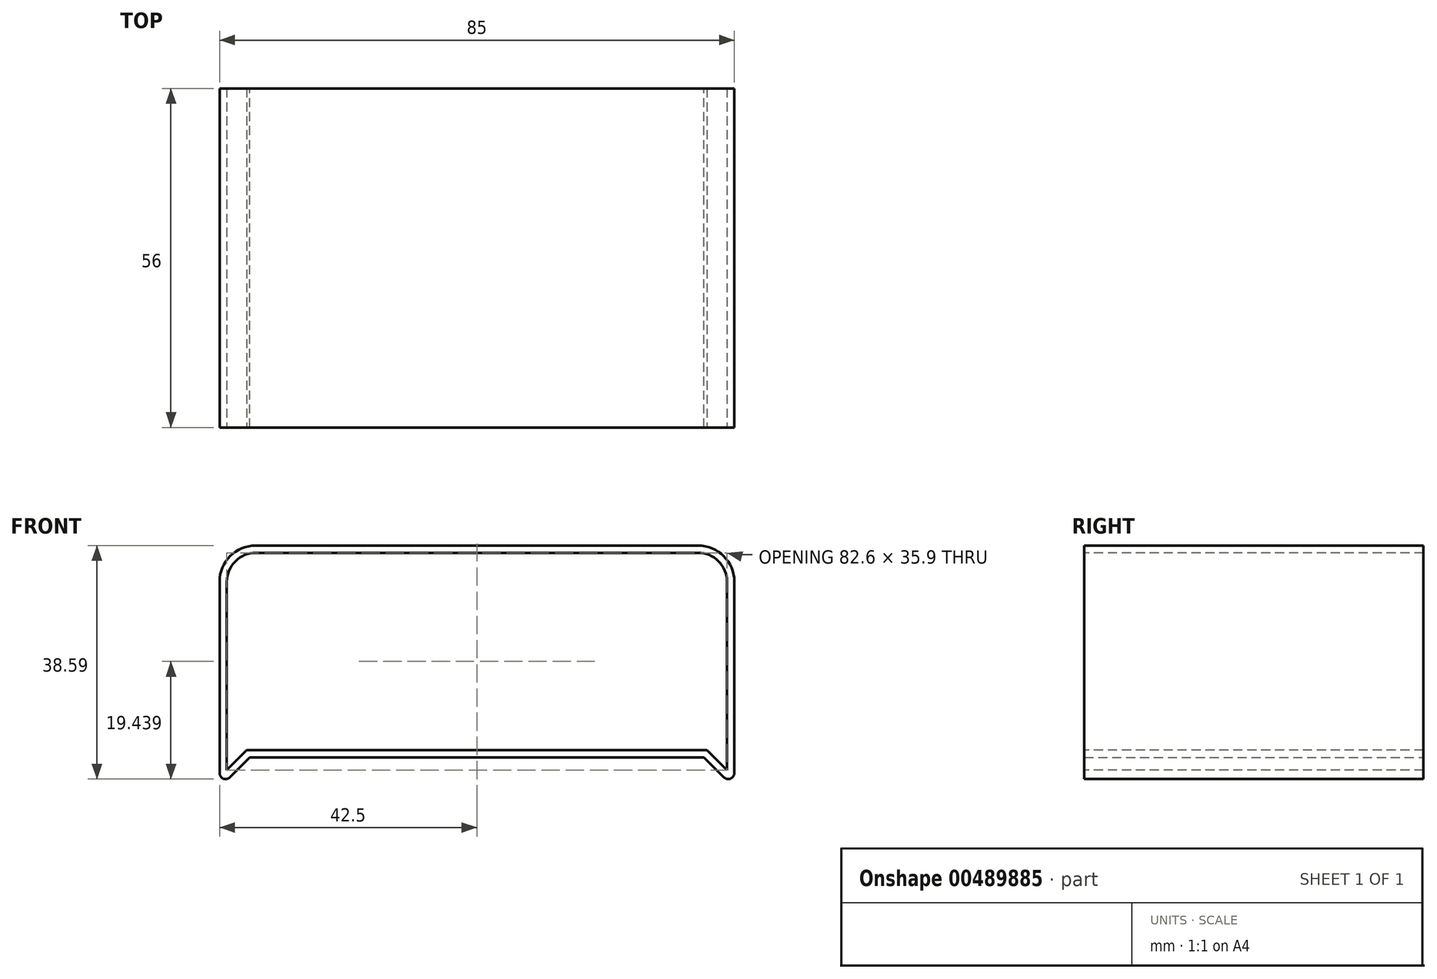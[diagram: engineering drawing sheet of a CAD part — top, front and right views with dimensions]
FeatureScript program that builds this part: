
annotation { "Feature Type Name" : "Feature", "Feature Type Description" : "" }
export const myFeature = defineFeature(function(context is Context, id is Id, definition is map)
    precondition{}
    {
        {
            var Q0;
            Q0=qCreatedBy(makeId("Front.planeOp"),FACE);
            var sketch = newSketch(context, id + "F0", { "sketchPlane" : qUnion([Q0])});
            skLineSegment(sketch, "E0.bottom", {"start": v(-42.5, 17.5) * mm, "end": v(42.5, 17.5) * mm});
            skLineSegment(sketch, "E0.top", {"start": v(-42.5, -17.5) * mm, "end": v(42.5, -17.5) * mm});
            skLineSegment(sketch, "E0.left", {"start": v(-42.5, 17.5) * mm, "end": v(-42.5, -17.5) * mm});
            skLineSegment(sketch, "E0.right", {"start": v(42.5, 17.5) * mm, "end": v(42.5, -17.5) * mm});
            skPoint(sketch, "E0.middle", {"position": v(0, 0) * mm});
            skLineSegment(sketch, "E1", {"start": v(-42.5, -17.5) * mm, "end": v(-42.5, -22.5) * mm});
            skLineSegment(sketch, "E2", {"start": v(-42.5, -22.5) * mm, "end": v(-37.5, -17.5) * mm});
            skLineSegment(sketch, "E3", {"start": v(42.5, -17.5) * mm, "end": v(42.5, -22.5) * mm});
            skLineSegment(sketch, "E4", {"start": v(42.5, -22.5) * mm, "end": v(37.5, -17.5) * mm});
            skSolve(sketch);
        }
        {
            var Q0;
            Q0 = qSketchRegion(id + "F0", true);
            extrude(context, id + "F1", {"entities" : qUnion([Q0]), "depth" : 56 * mm});
        }
        {
            var Q0;
            Q0=makeQuery(id+"F1.opExtrude","SWEPT_EDGE",EDGE,{"disambiguationData":[OSD([sQuery(id+"F0.wireOp",EDGE,"E1"),sQuery(id+"F0.wireOp",EDGE,"E2")])]});
            var Q1;
            Q1=makeQuery(id+"F1.opExtrude","SWEPT_EDGE",EDGE,{"disambiguationData":[OSD([sQuery(id+"F0.wireOp",EDGE,"E3"),sQuery(id+"F0.wireOp",EDGE,"E4")])]});
            fillet(context, id + "F2", {"entities" : qUnion([Q0, Q1]), "radius" : 1 * mm, "tangentPropagation" : true, "allowEdgeOverflow" : false});
        }
        {
            var Q0;
            Q0=makeQuery(id+"F1.opExtrude","SWEPT_EDGE",EDGE,{"disambiguationData":[OSD([sQuery(id+"F0.wireOp",EDGE,"E0.bottom"),sQuery(id+"F0.wireOp",EDGE,"E0.left")])]});
            var Q1;
            Q1=makeQuery(id+"F1.opExtrude","SWEPT_EDGE",EDGE,{"disambiguationData":[OSD([sQuery(id+"F0.wireOp",EDGE,"E0.bottom"),sQuery(id+"F0.wireOp",EDGE,"E0.right")])]});
            fillet(context, id + "F3", {"entities" : qUnion([Q0, Q1]), "radius" : 6 * mm, "tangentPropagation" : true, "allowEdgeOverflow" : false});
        }
        {
            var Q0;
            Q0=makeQuery(id+"F1.opExtrude","CAP_FACE",FACE,{"disambiguationData":[OSD([sQuery(id+"F0.wireOp",EDGE,"E0.bottom"),sQuery(id+"F0.wireOp",EDGE,"E0.top"),sQuery(id+"F0.wireOp",EDGE,"E0.left"),sQuery(id+"F0.wireOp",EDGE,"E0.right"),sQuery(id+"F0.wireOp",EDGE,"E1"),sQuery(id+"F0.wireOp",EDGE,"E2"),sQuery(id+"F0.wireOp",EDGE,"E3"),sQuery(id+"F0.wireOp",EDGE,"E4")])],"isStart":false});
            var sketch = newSketch(context, id + "F4", { "sketchPlane" : qUnion([Q0])});
            skLineSegment(sketch, "E5.0", {"start": v(38, -16.3) * mm, "end": v(41.3, -19.6) * mm});
            skLineSegment(sketch, "E5.1", {"start": v(-38, -16.3) * mm, "end": v(38, -16.3) * mm});
            skLineSegment(sketch, "E5.2", {"start": v(41.3, -19.6) * mm, "end": v(41.3, 11.5) * mm});
            skLineSegment(sketch, "E5.3", {"start": v(-41.3, -19.6) * mm, "end": v(-38, -16.3) * mm});
            skArc(sketch, "E5.4", {"start": v(41.3, 11.5) * mm, "mid": v(39.9, 14.9) * mm, "end": v(36.5, 16.3) * mm});
            skLineSegment(sketch, "E5.5", {"start": v(36.5, 16.3) * mm, "end": v(-36.5, 16.3) * mm});
            skArc(sketch, "E5.6", {"start": v(-36.5, 16.3) * mm, "mid": v(-39.9, 14.9) * mm, "end": v(-41.3, 11.5) * mm});
            skLineSegment(sketch, "E5.7", {"start": v(-41.3, 11.5) * mm, "end": v(-41.3, -19.6) * mm});
            skSolve(sketch);
        }
        {
            var Q0;
            Q0 = qSketchRegion(id + "F4", true);
            extrude(context, id + "F5", {"entities" : qUnion([Q0]), "operationType" : NewBodyOperationType.REMOVE, "oppositeDirection" : true, "depth" : 99.1 * mm});
        }
    });
